# Revit family: Boiler-Weil-McLain-150C
name_source: partatom
category: Mechanical Equipment
revit_build: Autodesk Revit 2018 (Build: 20190510_1515(x64)
units: mm (PartAtom-declared; Revit-internal decimal feet)

## family parameters
Always vertical = Yes
Cut with Voids When Loaded = No
OmniClass Number = 23.75.10.11.14.14
OmniClass Title = Condensing Boilers
Part Type = Normal
Room Calculation Point = No
Round Connector Dimension = Use Radius
Shared = No
Work Plane-Based = No

## types (3) — shared parameters
Air Vent Radius = 2"
Back Casing = Metal - Weil-Mclain - Paint Black
Boiler Water In = 1"
Boiler Water In Radius = 1"
Boiler Water Out = 1"
Boiler Water Out Radius = 0"
Clearance Depth = 18.46 "
Depth = 11 "
Feet = Plastic - Weil-Mclain - Plastic - White
Frequency = 60 Hz
Front Casing = Plastic - Weil-McLain - Paint Tan
Gas Connection Radius = 0"
Gas Connection Size = 1"
Height = 32.22 "
Manufacturer = Weil-McLain
Manufacturer Fax = 630-560-3769
Phase = 1
URL = https://www.weil-mclain.com
Voltage = 120 V
Warranty = https://www.weil-mclain.com
Width = 20 "

## type names (no varying parameters)
- 110-C
- 150-C
- 199-C

note: column(s) folded — value = type name in every type: Model

## geometry (parser evidence)
native form markers: Blend x18, Sweep x6
no freeform markers — native parametric forms only
